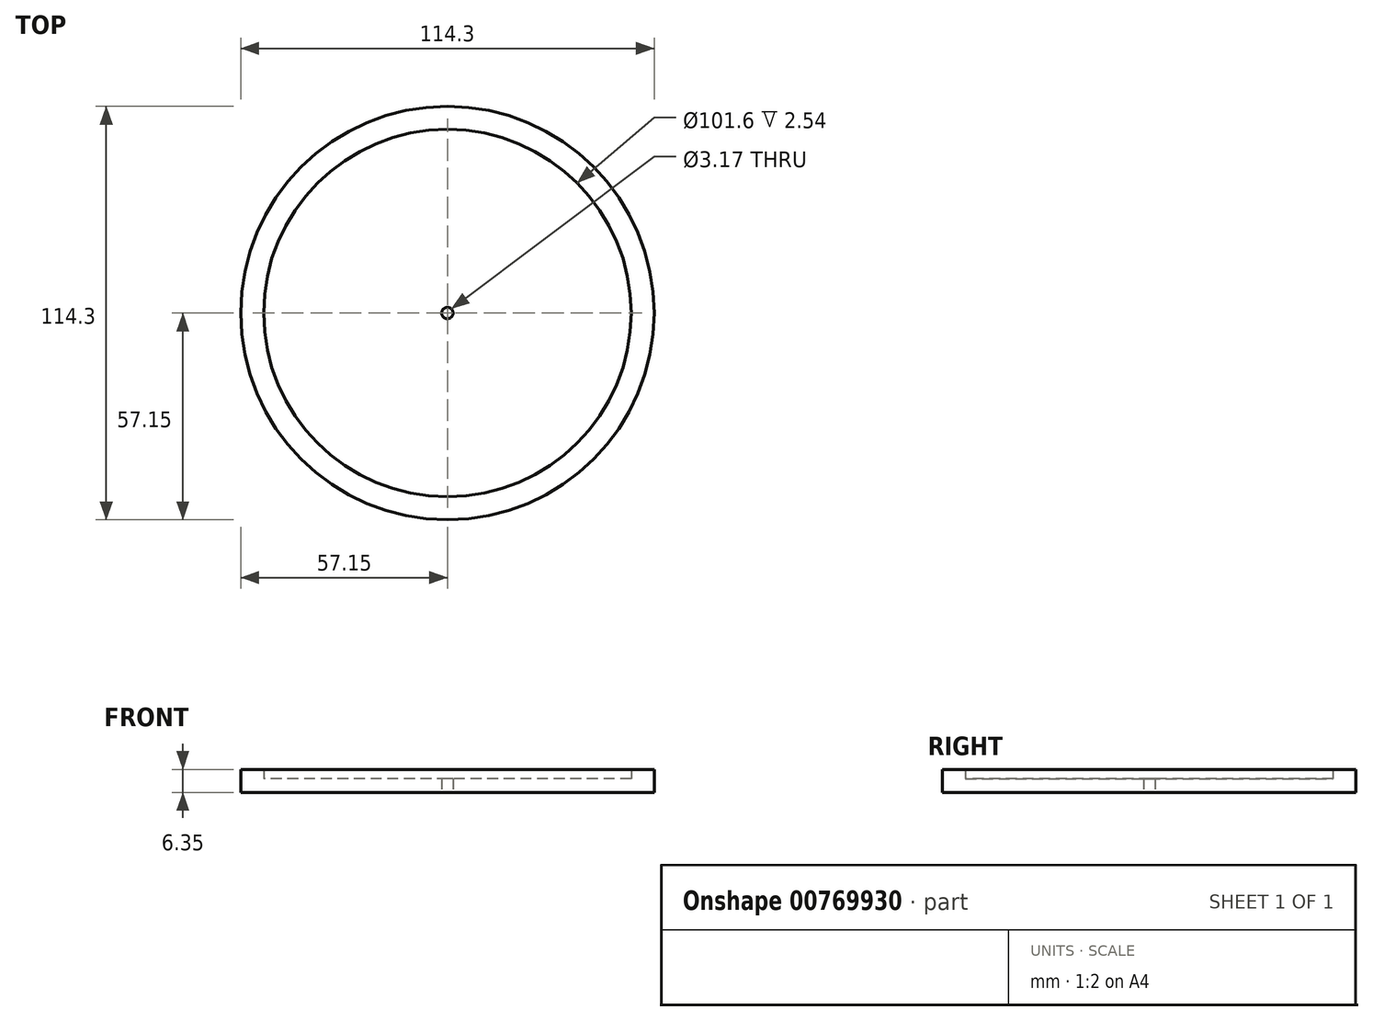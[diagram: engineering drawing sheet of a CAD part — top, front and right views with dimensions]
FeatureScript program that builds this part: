
annotation { "Feature Type Name" : "Feature", "Feature Type Description" : "" }
export const myFeature = defineFeature(function(context is Context, id is Id, definition is map)
    precondition{}
    {
        {
            var Q0;
            Q0=qCreatedBy(makeId("Top.planeOp"),FACE);
            var sketch = newSketch(context, id + "F0", { "sketchPlane" : qUnion([Q0])});
            skCircle(sketch, "E0", {"center": v(0, 0) * mm, "radius": 57.15 * mm});
            skCircle(sketch, "E1", {"center": v(0, 0) * mm, "radius": 50.8 * mm});
            skCircle(sketch, "E2", {"center": v(0, 0) * mm, "radius": 1.59 * mm});
            skLineSegment(sketch, "E3", {"start": v(0, 0) * mm, "end": v(-50.37, 6.63) * mm});
            skLineSegment(sketch, "E4", {"start": v(-50.37, 6.63) * mm, "end": v(0, 0) * mm});
            skLineSegment(sketch, "E5", {"start": v(0, 0) * mm, "end": v(-7.77, 50.2) * mm});
            skLineSegment(sketch, "E6", {"start": v(0, 0) * mm, "end": v(-42.25, 28.2) * mm});
            skLineSegment(sketch, "E7", {"start": v(-42.25, 28.2) * mm, "end": v(0, 0) * mm});
            skLineSegment(sketch, "E8", {"start": v(0, 0) * mm, "end": v(-31.84, 39.58) * mm});
            skLineSegment(sketch, "E9.MirrorCS", {"start": v(0, 0) * mm, "end": v(7.77, 50.2) * mm});
            skLineSegment(sketch, "E10.MirrorCS", {"start": v(0, 0) * mm, "end": v(31.84, 39.58) * mm});
            skLineSegment(sketch, "E11.MirrorCS", {"start": v(42.25, 28.2) * mm, "end": v(0, 0) * mm});
            skLineSegment(sketch, "E12.MirrorCS", {"start": v(50.37, 6.63) * mm, "end": v(0, 0) * mm});
            skLineSegment(sketch, "E13.MirrorCS", {"start": v(50.37, -6.63) * mm, "end": v(0, 0) * mm});
            skLineSegment(sketch, "E14.MirrorCS", {"start": v(42.25, -28.2) * mm, "end": v(0, 0) * mm});
            skLineSegment(sketch, "E15.MirrorCS", {"start": v(0, 0) * mm, "end": v(31.84, -39.58) * mm});
            skLineSegment(sketch, "E16.MirrorCS", {"start": v(0, 0) * mm, "end": v(7.77, -50.2) * mm});
            skLineSegment(sketch, "E17.MirrorCS", {"start": v(0, 0) * mm, "end": v(-31.84, -39.58) * mm});
            skLineSegment(sketch, "E18.MirrorCS", {"start": v(-42.25, -28.2) * mm, "end": v(0, 0) * mm});
            skLineSegment(sketch, "E19.MirrorCS", {"start": v(-50.37, -6.63) * mm, "end": v(0, 0) * mm});
            skLineSegment(sketch, "E20.MirrorCS", {"start": v(0, 0) * mm, "end": v(-7.77, -50.2) * mm});
            skCircle(sketch, "E21", {"center": v(0, 0) * mm, "radius": 12.36 * mm});
            skSolve(sketch);
        }
        {
            var Q0;
            Q0 = qSketchRegion(id + "F0", true);
            extrude(context, id + "F1", {"entities" : qUnion([Q0]), "depth" : 6.35 * mm, "offsetDistance" : 25.4 * mm});
        }
        {
            var Q0;
            Q0 = qSketchRegion(id + "F0", true);
            var Q1;
            {var subQ0=sQuery(id+"F0.wireOp",EDGE,"E7");var subQ1=sQuery(id+"F0.wireOp",EDGE,"E1");var subQ2=makeQuery(id+"F0.imprint","INTERSECT",VERTEX,{"derivedFrom":[subQ1,subQ0]});Q1=makeQuery(id+"F0.imprint","IMPRINT",FACE,{"disambiguationData":[TD([[makeQuery(id+"F0.imprint","IMPRINT",EDGE,{"disambiguationData":[TD([[subQ2,1.0]])],"derivedFrom":subQ1}),1.0]])]});}
            var Q2;
            {var subQ0=sQuery(id+"F0.wireOp",EDGE,"E5");var subQ1=sQuery(id+"F0.wireOp",EDGE,"E1");var subQ2=makeQuery(id+"F0.imprint","INTERSECT",VERTEX,{"derivedFrom":[subQ1,subQ0]});Q2=makeQuery(id+"F0.imprint","IMPRINT",FACE,{"disambiguationData":[TD([[makeQuery(id+"F0.imprint","IMPRINT",EDGE,{"disambiguationData":[TD([[subQ2,1.0]])],"derivedFrom":subQ1}),1.0]])]});}
            var Q3;
            {var subQ0=sQuery(id+"F0.wireOp",EDGE,"E10.MirrorCS");var subQ1=sQuery(id+"F0.wireOp",EDGE,"E1");var subQ2=makeQuery(id+"F0.imprint","INTERSECT",VERTEX,{"derivedFrom":[subQ1,subQ0]});Q3=makeQuery(id+"F0.imprint","IMPRINT",FACE,{"disambiguationData":[TD([[makeQuery(id+"F0.imprint","IMPRINT",EDGE,{"disambiguationData":[TD([[subQ2,1.0]])],"derivedFrom":subQ1}),1.0]])]});}
            var Q4;
            {var subQ0=sQuery(id+"F0.wireOp",EDGE,"E12.MirrorCS");var subQ1=sQuery(id+"F0.wireOp",EDGE,"E1");var subQ2=makeQuery(id+"F0.imprint","INTERSECT",VERTEX,{"derivedFrom":[subQ1,subQ0]});Q4=makeQuery(id+"F0.imprint","IMPRINT",FACE,{"disambiguationData":[TD([[makeQuery(id+"F0.imprint","IMPRINT",EDGE,{"disambiguationData":[TD([[subQ2,1.0]])],"derivedFrom":subQ1}),1.0]])]});}
            var Q5;
            {var subQ0=sQuery(id+"F0.wireOp",EDGE,"E14.MirrorCS");var subQ1=sQuery(id+"F0.wireOp",EDGE,"E1");var subQ2=makeQuery(id+"F0.imprint","INTERSECT",VERTEX,{"derivedFrom":[subQ1,subQ0]});Q5=makeQuery(id+"F0.imprint","IMPRINT",FACE,{"disambiguationData":[TD([[makeQuery(id+"F0.imprint","IMPRINT",EDGE,{"disambiguationData":[TD([[subQ2,1.0]])],"derivedFrom":subQ1}),1.0]])]});}
            var Q6;
            {var subQ0=sQuery(id+"F0.wireOp",EDGE,"E16.MirrorCS");var subQ1=sQuery(id+"F0.wireOp",EDGE,"E1");var subQ2=makeQuery(id+"F0.imprint","INTERSECT",VERTEX,{"derivedFrom":[subQ1,subQ0]});Q6=makeQuery(id+"F0.imprint","IMPRINT",FACE,{"disambiguationData":[TD([[makeQuery(id+"F0.imprint","IMPRINT",EDGE,{"disambiguationData":[TD([[subQ2,1.0]])],"derivedFrom":subQ1}),1.0]])]});}
            var Q7;
            {var subQ0=sQuery(id+"F0.wireOp",EDGE,"E17.MirrorCS");var subQ1=sQuery(id+"F0.wireOp",EDGE,"E1");var subQ2=makeQuery(id+"F0.imprint","INTERSECT",VERTEX,{"derivedFrom":[subQ1,subQ0]});Q7=makeQuery(id+"F0.imprint","IMPRINT",FACE,{"disambiguationData":[TD([[makeQuery(id+"F0.imprint","IMPRINT",EDGE,{"disambiguationData":[TD([[subQ2,1.0]])],"derivedFrom":subQ1}),1.0]])]});}
            var Q8;
            {var subQ0=sQuery(id+"F0.wireOp",EDGE,"E4");var subQ1=sQuery(id+"F0.wireOp",EDGE,"E1");var subQ2=makeQuery(id+"F0.imprint","INTERSECT",VERTEX,{"derivedFrom":[subQ1,subQ0]});Q8=makeQuery(id+"F0.imprint","IMPRINT",FACE,{"disambiguationData":[TD([[makeQuery(id+"F0.imprint","IMPRINT",EDGE,{"disambiguationData":[TD([[subQ2,-1.0]])],"derivedFrom":subQ1}),1.0]])]});}
            var Q9;
            {var subQ0=sQuery(id+"F0.wireOp",EDGE,"E16.MirrorCS");var subQ1=sQuery(id+"F0.wireOp",EDGE,"E2");var subQ2=makeQuery(id+"F0.imprint","INTERSECT",VERTEX,{"derivedFrom":[subQ1,subQ0]});Q9=makeQuery(id+"F0.imprint","IMPRINT",FACE,{"disambiguationData":[TD([[makeQuery(id+"F0.imprint","IMPRINT",EDGE,{"disambiguationData":[TD([[subQ2,-1.0]])],"derivedFrom":subQ1}),-1.0]])]});}
            var Q10;
            {var subQ0=sQuery(id+"F0.wireOp",EDGE,"E14.MirrorCS");var subQ1=sQuery(id+"F0.wireOp",EDGE,"E2");var subQ2=makeQuery(id+"F0.imprint","INTERSECT",VERTEX,{"derivedFrom":[subQ1,subQ0]});Q10=makeQuery(id+"F0.imprint","IMPRINT",FACE,{"disambiguationData":[TD([[makeQuery(id+"F0.imprint","IMPRINT",EDGE,{"disambiguationData":[TD([[subQ2,-1.0]])],"derivedFrom":subQ1}),-1.0]])]});}
            var Q11;
            {var subQ0=sQuery(id+"F0.wireOp",EDGE,"E11.MirrorCS");var subQ1=sQuery(id+"F0.wireOp",EDGE,"E2");var subQ2=makeQuery(id+"F0.imprint","INTERSECT",VERTEX,{"derivedFrom":[subQ1,subQ0]});Q11=makeQuery(id+"F0.imprint","IMPRINT",FACE,{"disambiguationData":[TD([[makeQuery(id+"F0.imprint","IMPRINT",EDGE,{"disambiguationData":[TD([[subQ2,1.0]])],"derivedFrom":subQ1}),-1.0]])]});}
            var Q12;
            {var subQ0=sQuery(id+"F0.wireOp",EDGE,"E10.MirrorCS");var subQ1=sQuery(id+"F0.wireOp",EDGE,"E2");var subQ2=makeQuery(id+"F0.imprint","INTERSECT",VERTEX,{"derivedFrom":[subQ1,subQ0]});Q12=makeQuery(id+"F0.imprint","IMPRINT",FACE,{"disambiguationData":[TD([[makeQuery(id+"F0.imprint","IMPRINT",EDGE,{"disambiguationData":[TD([[subQ2,-1.0]])],"derivedFrom":subQ1}),-1.0]])]});}
            var Q13;
            {var subQ0=sQuery(id+"F0.wireOp",EDGE,"E5");var subQ1=sQuery(id+"F0.wireOp",EDGE,"E2");var subQ2=makeQuery(id+"F0.imprint","INTERSECT",VERTEX,{"derivedFrom":[subQ1,subQ0]});Q13=makeQuery(id+"F0.imprint","IMPRINT",FACE,{"disambiguationData":[TD([[makeQuery(id+"F0.imprint","IMPRINT",EDGE,{"disambiguationData":[TD([[subQ2,-1.0]])],"derivedFrom":subQ1}),-1.0]])]});}
            var Q14;
            {var subQ0=sQuery(id+"F0.wireOp",EDGE,"E7");var subQ1=sQuery(id+"F0.wireOp",EDGE,"E2");var subQ2=makeQuery(id+"F0.imprint","INTERSECT",VERTEX,{"derivedFrom":[subQ1,subQ0]});Q14=makeQuery(id+"F0.imprint","IMPRINT",FACE,{"disambiguationData":[TD([[makeQuery(id+"F0.imprint","IMPRINT",EDGE,{"disambiguationData":[TD([[subQ2,-1.0]])],"derivedFrom":subQ1}),-1.0]])]});}
            var Q15;
            {var subQ0=sQuery(id+"F0.wireOp",EDGE,"E17.MirrorCS");var subQ1=sQuery(id+"F0.wireOp",EDGE,"E2");var subQ2=makeQuery(id+"F0.imprint","INTERSECT",VERTEX,{"derivedFrom":[subQ1,subQ0]});Q15=makeQuery(id+"F0.imprint","IMPRINT",FACE,{"disambiguationData":[TD([[makeQuery(id+"F0.imprint","IMPRINT",EDGE,{"disambiguationData":[TD([[subQ2,-1.0]])],"derivedFrom":subQ1}),-1.0]])]});}
            var Q16;
            {var subQ0=sQuery(id+"F0.wireOp",EDGE,"E20.MirrorCS");var subQ1=sQuery(id+"F0.wireOp",EDGE,"E2");var subQ2=makeQuery(id+"F0.imprint","INTERSECT",VERTEX,{"derivedFrom":[subQ1,subQ0]});Q16=makeQuery(id+"F0.imprint","IMPRINT",FACE,{"disambiguationData":[TD([[makeQuery(id+"F0.imprint","IMPRINT",EDGE,{"disambiguationData":[TD([[subQ2,-1.0]])],"derivedFrom":subQ1}),-1.0]])]});}
            var Q17;
            {var subQ0=sQuery(id+"F0.wireOp",EDGE,"E15.MirrorCS");var subQ1=sQuery(id+"F0.wireOp",EDGE,"E2");var subQ2=makeQuery(id+"F0.imprint","INTERSECT",VERTEX,{"derivedFrom":[subQ1,subQ0]});Q17=makeQuery(id+"F0.imprint","IMPRINT",FACE,{"disambiguationData":[TD([[makeQuery(id+"F0.imprint","IMPRINT",EDGE,{"disambiguationData":[TD([[subQ2,-1.0]])],"derivedFrom":subQ1}),-1.0]])]});}
            var Q18;
            {var subQ0=sQuery(id+"F0.wireOp",EDGE,"E12.MirrorCS");var subQ1=sQuery(id+"F0.wireOp",EDGE,"E2");var subQ2=makeQuery(id+"F0.imprint","INTERSECT",VERTEX,{"derivedFrom":[subQ1,subQ0]});Q18=makeQuery(id+"F0.imprint","IMPRINT",FACE,{"disambiguationData":[TD([[makeQuery(id+"F0.imprint","IMPRINT",EDGE,{"disambiguationData":[TD([[subQ2,1.0]])],"derivedFrom":subQ1}),-1.0]])]});}
            var Q19;
            {var subQ0=sQuery(id+"F0.wireOp",EDGE,"E11.MirrorCS");var subQ1=sQuery(id+"F0.wireOp",EDGE,"E2");var subQ2=makeQuery(id+"F0.imprint","INTERSECT",VERTEX,{"derivedFrom":[subQ1,subQ0]});Q19=makeQuery(id+"F0.imprint","IMPRINT",FACE,{"disambiguationData":[TD([[makeQuery(id+"F0.imprint","IMPRINT",EDGE,{"disambiguationData":[TD([[subQ2,-1.0]])],"derivedFrom":subQ1}),-1.0]])]});}
            var Q20;
            {var subQ0=sQuery(id+"F0.wireOp",EDGE,"E9.MirrorCS");var subQ1=sQuery(id+"F0.wireOp",EDGE,"E2");var subQ2=makeQuery(id+"F0.imprint","INTERSECT",VERTEX,{"derivedFrom":[subQ1,subQ0]});Q20=makeQuery(id+"F0.imprint","IMPRINT",FACE,{"disambiguationData":[TD([[makeQuery(id+"F0.imprint","IMPRINT",EDGE,{"disambiguationData":[TD([[subQ2,-1.0]])],"derivedFrom":subQ1}),-1.0]])]});}
            var Q21;
            {var subQ0=sQuery(id+"F0.wireOp",EDGE,"E8");var subQ1=sQuery(id+"F0.wireOp",EDGE,"E2");var subQ2=makeQuery(id+"F0.imprint","INTERSECT",VERTEX,{"derivedFrom":[subQ1,subQ0]});Q21=makeQuery(id+"F0.imprint","IMPRINT",FACE,{"disambiguationData":[TD([[makeQuery(id+"F0.imprint","IMPRINT",EDGE,{"disambiguationData":[TD([[subQ2,-1.0]])],"derivedFrom":subQ1}),-1.0]])]});}
            var Q22;
            {var subQ0=sQuery(id+"F0.wireOp",EDGE,"E18.MirrorCS");var subQ1=sQuery(id+"F0.wireOp",EDGE,"E2");var subQ2=makeQuery(id+"F0.imprint","INTERSECT",VERTEX,{"derivedFrom":[subQ1,subQ0]});Q22=makeQuery(id+"F0.imprint","IMPRINT",FACE,{"disambiguationData":[TD([[makeQuery(id+"F0.imprint","IMPRINT",EDGE,{"disambiguationData":[TD([[subQ2,-1.0]])],"derivedFrom":subQ1}),-1.0]])]});}
            var Q23;
            {var subQ0=sQuery(id+"F0.wireOp",EDGE,"E4");var subQ1=sQuery(id+"F0.wireOp",EDGE,"E2");var subQ2=makeQuery(id+"F0.imprint","INTERSECT",VERTEX,{"derivedFrom":[subQ1,subQ0]});Q23=makeQuery(id+"F0.imprint","IMPRINT",FACE,{"disambiguationData":[TD([[makeQuery(id+"F0.imprint","IMPRINT",EDGE,{"disambiguationData":[TD([[subQ2,-1.0]])],"derivedFrom":subQ1}),-1.0]])]});}
            var Q24;
            {var subQ0=sQuery(id+"F0.wireOp",EDGE,"E19.MirrorCS");var subQ1=sQuery(id+"F0.wireOp",EDGE,"E2");var subQ2=makeQuery(id+"F0.imprint","INTERSECT",VERTEX,{"derivedFrom":[subQ1,subQ0]});Q24=makeQuery(id+"F0.imprint","IMPRINT",FACE,{"disambiguationData":[TD([[makeQuery(id+"F0.imprint","IMPRINT",EDGE,{"disambiguationData":[TD([[subQ2,-1.0]])],"derivedFrom":subQ1}),-1.0]])]});}
            extrude(context, id + "F2", {"entities" : qUnion([Q0, Q1, Q2, Q3, Q4, Q5, Q6, Q7, Q8, Q9, Q10, Q11, Q12, Q13, Q14, Q15, Q16, Q17, Q18, Q19, Q20, Q21, Q22, Q23, Q24]), "operationType" : NewBodyOperationType.ADD, "depth" : 3.8 * mm, "offsetDistance" : 25.4 * mm});
        }
    });
